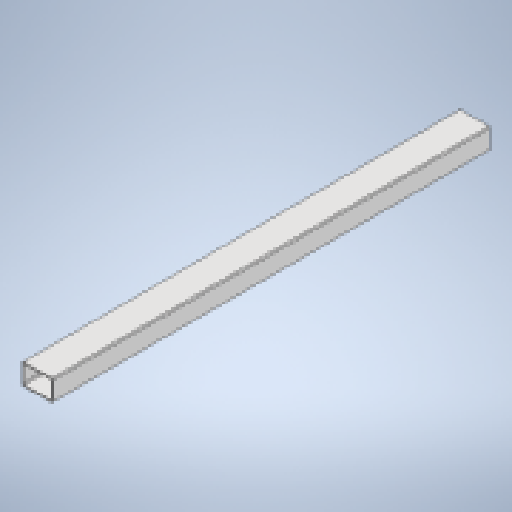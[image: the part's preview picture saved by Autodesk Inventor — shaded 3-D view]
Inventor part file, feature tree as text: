
AUTODESK INVENTOR PART (.ipt)
format: ipt  version: 2023 (Build 270158000, 158)  size: 152,576 bytes
history: native  units: in
note: dims shown in document units (in); Inventor stores cm internally (conversion verified against a paired STEP export)
features: extrude x1, shell x1, fillet x1, sketch x1
ambient origin geometry x8: Origin, YZ Plane, XZ Plane, XY Plane, X Axis, Y Axis, Z Axis, Center Point
bodies: Solid1 (feature_tree)
feature tree (4):
  extrude  "Extrusion1"  Depth=2.0in
  shell  "Shell1"  Thickness=48.0in
  fillet  "Fillet1"  Radius=0.125in
  sketch  "Sketch1"  dims[d0=3.0in d1=2.0in d2=48.0in d3=0.0in d4=0.125in d5=0.125in]
